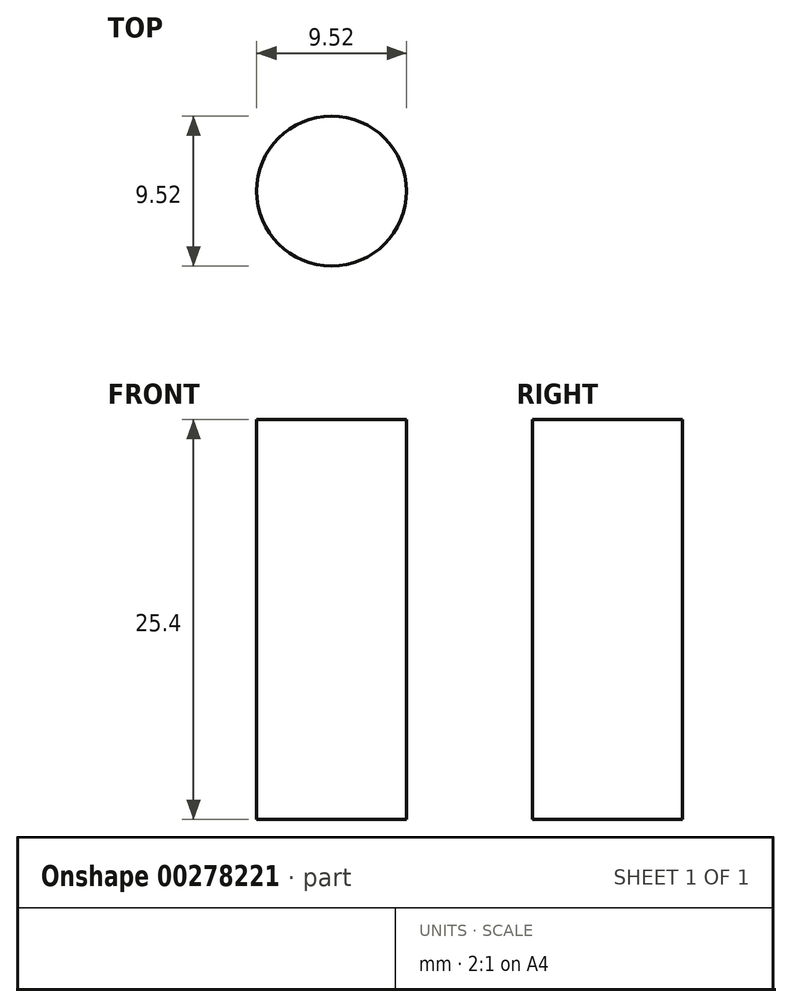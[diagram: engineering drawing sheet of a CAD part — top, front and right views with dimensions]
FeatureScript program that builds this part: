
annotation { "Feature Type Name" : "Feature", "Feature Type Description" : "" }
export const myFeature = defineFeature(function(context is Context, id is Id, definition is map)
    precondition{}
    {
        {
            var Q0;
            Q0=qCreatedBy(makeId("Top.planeOp"),FACE);
            var sketch = newSketch(context, id + "F0", { "sketchPlane" : qUnion([Q0])});
            skCircle(sketch, "E0", {"center": v(0, 0) * mm, "radius": 4.76 * mm});
            skSolve(sketch);
        }
        {
            var Q0;
            Q0 = qSketchRegion(id + "F0", true);
            extrude(context, id + "F1", {"entities" : qUnion([Q0]), "depth" : 25.4 * mm});
        }
    });
